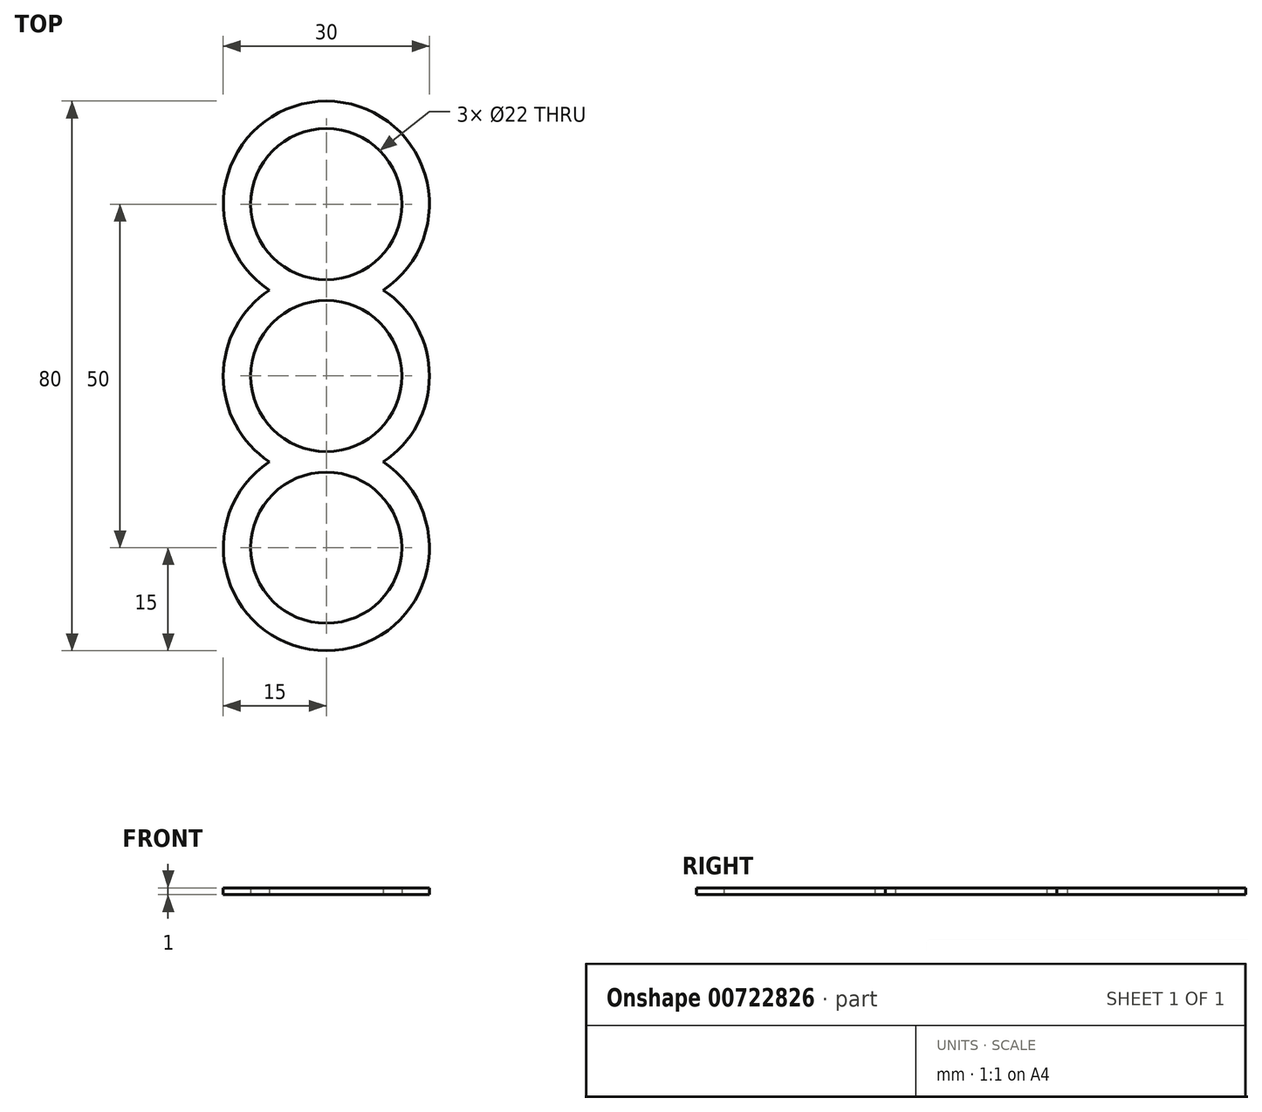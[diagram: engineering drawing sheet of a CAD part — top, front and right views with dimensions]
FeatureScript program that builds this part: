
annotation { "Feature Type Name" : "Feature", "Feature Type Description" : "" }
export const myFeature = defineFeature(function(context is Context, id is Id, definition is map)
    precondition{}
    {
        {
            var Q0;
            Q0=qCreatedBy(makeId("Top.planeOp"),FACE);
            var sketch = newSketch(context, id + "F0", { "sketchPlane" : qUnion([Q0])});
            skCircle(sketch, "E0", {"center": v(0, 0) * mm, "radius": 11 * mm});
            skCircle(sketch, "E1", {"center": v(0, 25) * mm, "radius": 11 * mm});
            skArc(sketch, "E2", {"start": v(8.3, 12.5) * mm, "mid": v(0, 40) * mm, "end": v(-8.3, 12.5) * mm});
            skArc(sketch, "E3", {"start": v(-8.3, 12.5) * mm, "mid": v(-15, 0) * mm, "end": v(-8.3, -12.5) * mm});
            skLineSegment(sketch, "E4", {"start": v(0, -14) * mm, "end": v(0, -15) * mm});
            skPoint(sketch, "E4.endSnap0", {"position": v(0, -15) * mm});
            skCircle(sketch, "E5", {"center": v(0, -25) * mm, "radius": 11 * mm});
            skArc(sketch, "E6", {"start": v(-8.3, -12.5) * mm, "mid": v(0, -40) * mm, "end": v(8.3, -12.5) * mm});
            skArc(sketch, "E7.trimOffspring", {"start": v(8.3, -12.5) * mm, "mid": v(15, 0) * mm, "end": v(8.3, 12.5) * mm});
            skSolve(sketch);
        }
        {
            var Q0;
            Q0=makeQuery(id+"F0.imprint","IMPRINT",FACE,{"disambiguationData":[TD([[makeQuery(id+"F0.imprint","IMPRINT",EDGE,{"derivedFrom":sQuery(id+"F0.wireOp",EDGE,"E0")}),-1.0]])]});
            extrude(context, id + "F1", {"entities" : qUnion([Q0]), "depth" : 1 * mm, "offsetDistance" : 25 * mm});
        }
    });
